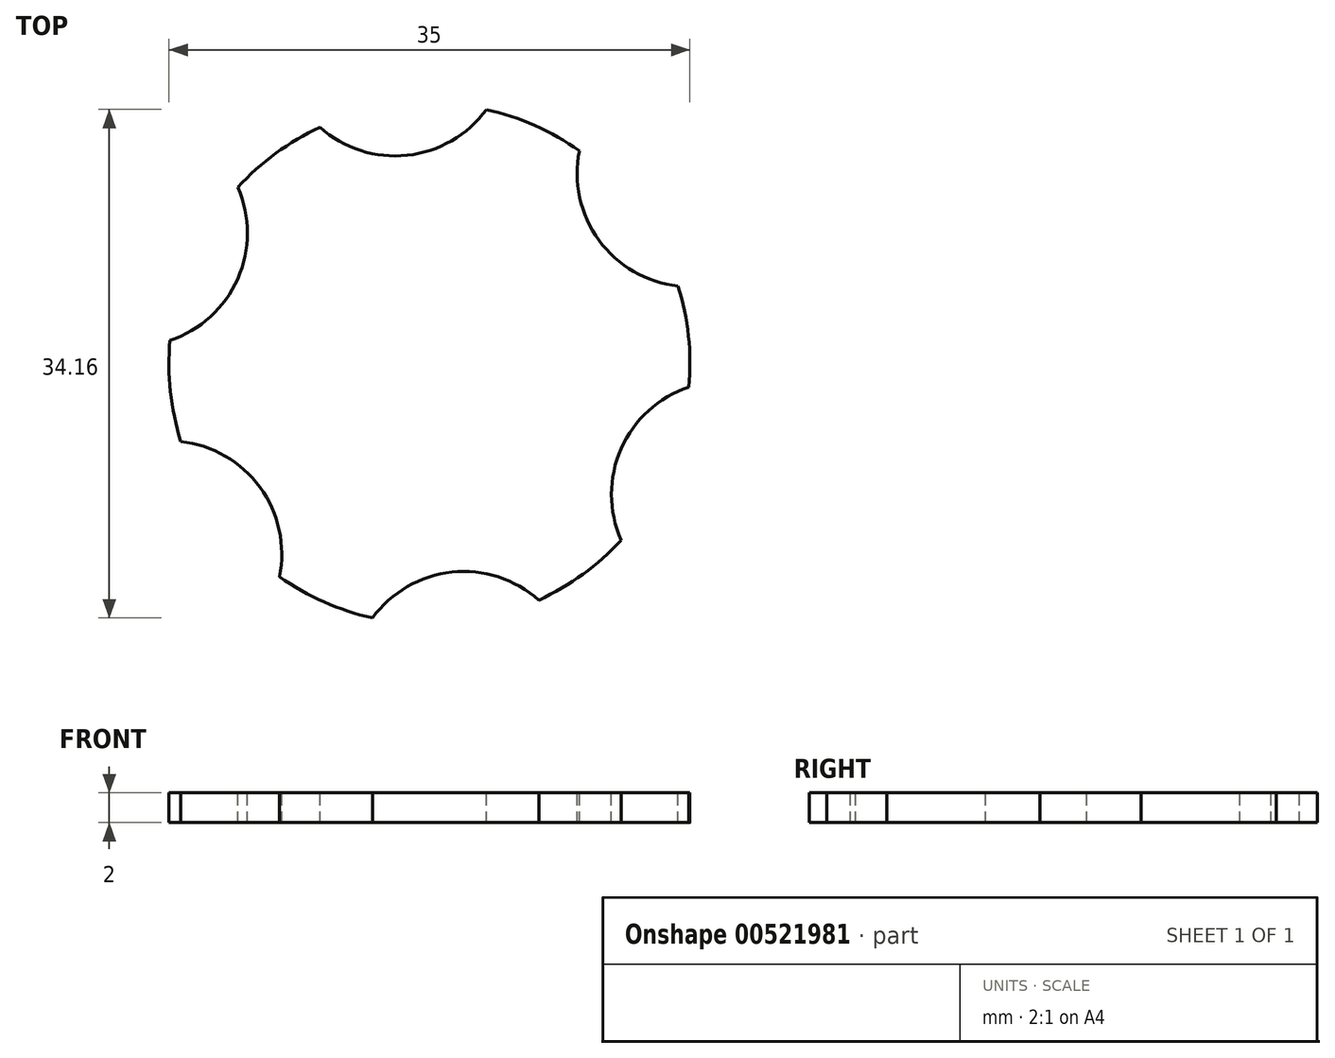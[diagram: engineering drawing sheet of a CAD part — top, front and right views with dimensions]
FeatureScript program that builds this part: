
annotation { "Feature Type Name" : "Feature", "Feature Type Description" : "" }
export const myFeature = defineFeature(function(context is Context, id is Id, definition is map)
    precondition{}
    {
        {
            var Q0;
            Q0=qCreatedBy(makeId("Top.planeOp"),FACE);
            var sketch = newSketch(context, id + "F0", { "sketchPlane" : qUnion([Q0])});
            skCircle(sketch, "E0", {"center": v(0, 0) * mm, "radius": 17.5 * mm});
            skSolve(sketch);
        }
        {
            var Q0;
            Q0=makeQuery(id+"F0.imprint","IMPRINT",FACE,{"disambiguationData":[TD([[makeQuery(id+"F0.imprint","IMPRINT",EDGE,{"derivedFrom":sQuery(id+"F0.wireOp",EDGE,"E0")}),1.0]])]});
            extrude(context, id + "F1", {"entities" : qUnion([Q0]), "depth" : 2 * mm, "offsetDistance" : 25 * mm});
        }
        {
            var Q0;
            Q0=qCreatedBy(makeId("Top.planeOp"),FACE);
            var sketch = newSketch(context, id + "F2", { "sketchPlane" : qUnion([Q0])});
            skCircle(sketch, "E1", {"center": v(-19.83, 8.78) * mm, "radius": 7.6 * mm});
            skCircle(sketch, "E2.1.0", {"center": v(-17.52, -12.78) * mm, "radius": 7.6 * mm});
            skCircle(sketch, "E2.2.0", {"center": v(2.3, -21.56) * mm, "radius": 7.6 * mm});
            skCircle(sketch, "E2.3.0", {"center": v(19.83, -8.78) * mm, "radius": 7.6 * mm});
            skCircle(sketch, "E2.4.0", {"center": v(17.52, 12.78) * mm, "radius": 7.6 * mm});
            skCircle(sketch, "E2.5.0", {"center": v(-2.3, 21.56) * mm, "radius": 7.6 * mm});
            skPoint(sketch, "E2.center", {"position": v(0, 0) * mm});
            skSolve(sketch);
        }
        {
            var Q0;
            Q0 = qSketchRegion(id + "F2", true);
            extrude(context, id + "F3", {"entities" : qUnion([Q0]), "operationType" : NewBodyOperationType.REMOVE, "endBound" : BoundingType.SYMMETRIC, "oppositeDirection" : true, "depth" : 25 * mm, "offsetDistance" : 25 * mm});
        }
    });
